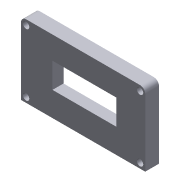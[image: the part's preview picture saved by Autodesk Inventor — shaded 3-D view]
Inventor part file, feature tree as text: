
AUTODESK INVENTOR PART (.ipt)
format: ipt  version: 2020 (Build 240168000, 168)  size: 345,088 bytes
history: native  units: in
note: dims shown in document units (in); Inventor stores cm internally (conversion verified against a paired STEP export)
features: reference x14, sketch x8, other x5, extrude x4, hole x2, plane x2, fillet x1, chamfer x1, helix x1
ambient origin geometry x8: Origin, YZ Plane, XZ Plane, XY Plane, X Axis, Y Axis, Z Axis, Center Point
bodies: Solid1 (feature_tree)
feature tree (38):
  extrude  "Extrusion1"  Depth=4.5in
  hole  "Hole2"  [1 undecoded]
  fillet  "Fillet1"  Radius=0.02in
  sketch  "Sketch3"  dims[d16=0.129in d17=0.75in d18=0.23in d19=0.375in d20=0.5635in d21=1.0in d22=0.8108in d23=0.02in]
  plane  "Work Plane1"
  extrude  "Extrusion4"  Depth=0.015in
  extrude  "Extrusion5"  Depth=0.04in
  extrude  "Extrusion6"  Depth=0.2in TaperAngle=0.0deg
  sketch  "Sketch8"  dims[d33=0.089in d34=0.75in d35=0.23in d36=0.375in d37=0.5635in d38=0.25in d39=0.0in d40=0.0125in d41=0.125in d42=45.0deg]
  hole  "Hole3"  [1 undecoded]
  chamfer  "Chamfer1"  Distance=0.0188in
  plane  "Work Plane2"
  helix  "Coil1"  [1 undecoded]
  sketch  "Sketch Driven Pattern1"  dims[d0=0.45in d1=0.0in d2=4.5in]
  sketch  "Sketch1"  dims[d3=2.621in d11=0.1875in]
  sketch  "Sketch5"  dims[d24=1.0in d25=0.0in d26=0.015in]
  reference  "Reference5"
  reference  "Reference6"
  reference  "Reference7"
  reference  "Reference8"
  reference  "Reference9"
  reference  "Reference10"
  reference  "Reference11"
  reference  "Reference12"
  sketch  "Sketch6"  dims[d27=0.0in d28=0.0in d29=0.04in]
  reference  "Reference13"
  reference  "Reference14"
  sketch  "Sketch7"  dims[d30=0.04in d31=0.2in d32=0.0in]
  reference  "Reference15"
  reference  "Reference16"
  reference  "Reference17"
  reference  "Reference18"
  sketch  "Sketch9"  dims[d43=60.0deg d44=0.0188in d45=0.0063in d46=0.2687in d47=0.025in d48=0.2687in d49=0.3937in d50=0.0in d51=90.0deg d52=90.0deg d53=0.0in d54=0.0in]
  other  "Readout.iam"
  other  "Readout Cover:1"
  other  "Base2:1"
  other  "4x20 LCD:4"
  other  "16 pin header:1"
note: 3 required parameter values undecoded (feature->parameter linkage not recoverable at this tier; creation-order binding heuristic only, values carry confidence <= 0.55)
